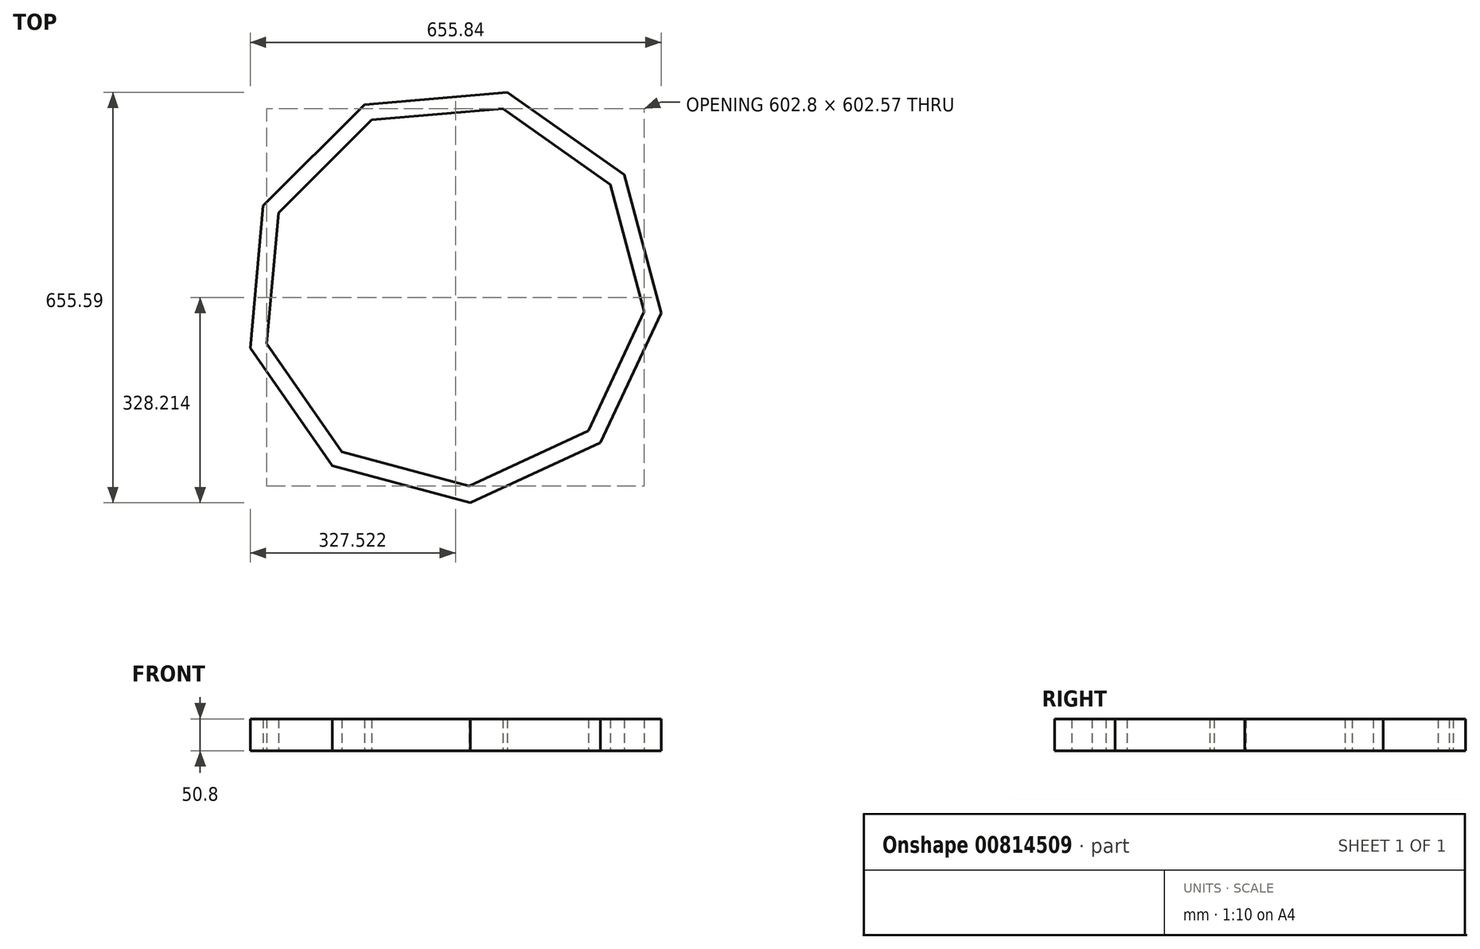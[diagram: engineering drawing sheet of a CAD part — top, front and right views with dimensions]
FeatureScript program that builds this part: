
annotation { "Feature Type Name" : "Feature", "Feature Type Description" : "" }
export const myFeature = defineFeature(function(context is Context, id is Id, definition is map)
    precondition{}
    {
        {
            var Q0;
            Q0=qCreatedBy(makeId("Top.planeOp"),FACE);
            var sketch = newSketch(context, id + "F0", { "sketchPlane" : qUnion([Q0])});
            skCircle(sketch, "E0.cCircle", {"center": v(0, 0) * mm, "radius": 314.04 * mm, "construction": true});
            skLineSegment(sketch, "E0.0", {"start": v(-140.57, 303.2) * mm, "end": v(87.2, 322.61) * mm});
            skLineSegment(sketch, "E0.1", {"start": v(87.2, 322.61) * mm, "end": v(274.17, 191.08) * mm});
            skLineSegment(sketch, "E0.2", {"start": v(274.17, 191.08) * mm, "end": v(332.85, -29.86) * mm});
            skLineSegment(sketch, "E0.3", {"start": v(332.85, -29.86) * mm, "end": v(235.79, -236.83) * mm});
            skLineSegment(sketch, "E0.4", {"start": v(235.79, -236.83) * mm, "end": v(28.4, -332.98) * mm});
            skLineSegment(sketch, "E0.5", {"start": v(28.4, -332.98) * mm, "end": v(-192.29, -273.33) * mm});
            skLineSegment(sketch, "E0.6", {"start": v(-192.29, -273.33) * mm, "end": v(-323, -85.78) * mm});
            skLineSegment(sketch, "E0.7", {"start": v(-323, -85.78) * mm, "end": v(-302.57, 141.9) * mm});
            skLineSegment(sketch, "E0.8", {"start": v(-302.57, 141.9) * mm, "end": v(-140.57, 303.2) * mm});
            skPoint(sketch, "E0.0.midPoint", {"position": v(-26.68, 312.9) * mm});
            skSolve(sketch);
        }
        {
            var Q0;
            Q0 = qSketchRegion(id + "F0", true);
            extrude(context, id + "F1", {"entities" : qUnion([Q0]), "depth" : 50.8 * mm, "offsetDistance" : 25.4 * mm});
        }
        {
            var Q0;
            Q0=makeQuery(id+"F1.opExtrude","CAP_FACE",FACE,{"disambiguationData":[OSD([sQuery(id+"F0.wireOp",EDGE,"E0.0"),sQuery(id+"F0.wireOp",EDGE,"E0.1"),sQuery(id+"F0.wireOp",EDGE,"E0.2"),sQuery(id+"F0.wireOp",EDGE,"E0.3"),sQuery(id+"F0.wireOp",EDGE,"E0.4"),sQuery(id+"F0.wireOp",EDGE,"E0.5"),sQuery(id+"F0.wireOp",EDGE,"E0.6"),sQuery(id+"F0.wireOp",EDGE,"E0.7"),sQuery(id+"F0.wireOp",EDGE,"E0.8")])],"isStart":true});
            var Q1;
            Q1=makeQuery(id+"F1.opExtrude","CAP_FACE",FACE,{"disambiguationData":[OSD([sQuery(id+"F0.wireOp",EDGE,"E0.0"),sQuery(id+"F0.wireOp",EDGE,"E0.1"),sQuery(id+"F0.wireOp",EDGE,"E0.2"),sQuery(id+"F0.wireOp",EDGE,"E0.3"),sQuery(id+"F0.wireOp",EDGE,"E0.4"),sQuery(id+"F0.wireOp",EDGE,"E0.5"),sQuery(id+"F0.wireOp",EDGE,"E0.6"),sQuery(id+"F0.wireOp",EDGE,"E0.7"),sQuery(id+"F0.wireOp",EDGE,"E0.8")])],"isStart":false});
            shell(context, id + "F2", {"entities" : qUnion([Q0, Q1]), "thickness" : 25.4 * mm});
        }
    });
